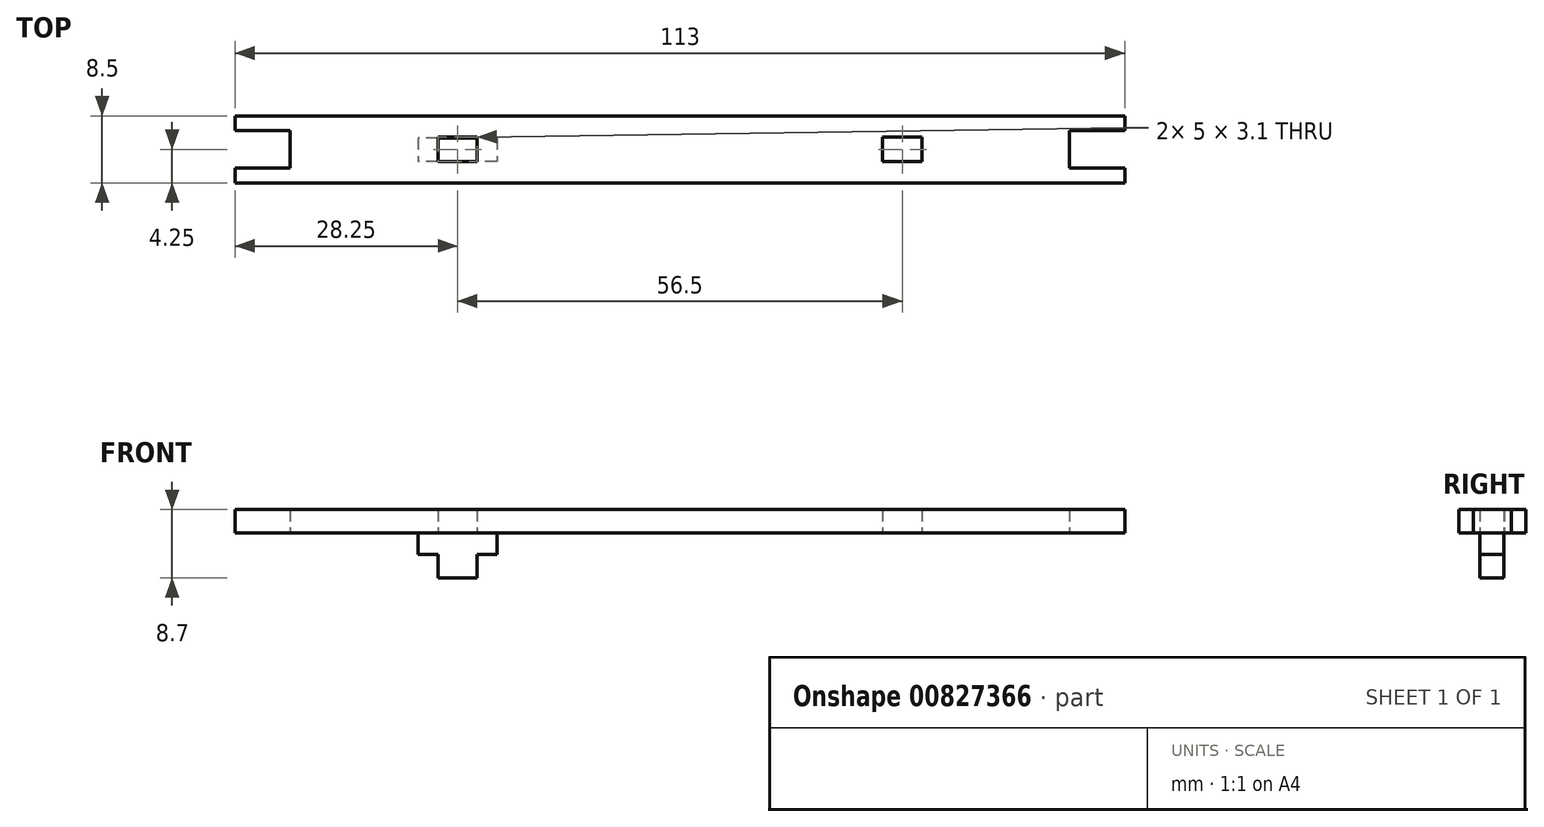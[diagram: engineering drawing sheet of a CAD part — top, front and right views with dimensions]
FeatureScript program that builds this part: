
annotation { "Feature Type Name" : "Feature", "Feature Type Description" : "" }
export const myFeature = defineFeature(function(context is Context, id is Id, definition is map)
    precondition{}
    {
        {
            var Q0;
            Q0=qCreatedBy(makeId("Top.planeOp"),FACE);
            var sketch = newSketch(context, id + "F0", { "sketchPlane" : qUnion([Q0])});
            skLineSegment(sketch, "E0.bottom", {"start": v(0, 4.25) * mm, "end": v(-56.5, 4.25) * mm});
            skLineSegment(sketch, "E0.top", {"start": v(0, -4.25) * mm, "end": v(-56.5, -4.25) * mm});
            skLineSegment(sketch, "E0.left", {"start": v(0, 4.25) * mm, "end": v(0, -4.25) * mm});
            skLineSegment(sketch, "E0.right", {"start": v(-56.5, 4.25) * mm, "end": v(-56.5, -4.25) * mm});
            skPoint(sketch, "E0.middle", {"position": v(-28.25, 0) * mm});
            skCircle(sketch, "E1", {"center": v(-47.98, 8.7) * mm, "radius": 2.6 * mm});
            skCircle(sketch, "E2", {"center": v(-47.98, 8.7) * mm, "radius": 1.35 * mm, "construction": true});
            skLineSegment(sketch, "E3", {"start": v(-50.2, 10.05) * mm, "end": v(-45.76, 10.05) * mm});
            skLineSegment(sketch, "E4.bottom", {"start": v(-25.75, 1.55) * mm, "end": v(-30.75, 1.55) * mm});
            skLineSegment(sketch, "E4.top", {"start": v(-25.75, -1.55) * mm, "end": v(-30.75, -1.55) * mm});
            skLineSegment(sketch, "E4.left", {"start": v(-25.75, 1.55) * mm, "end": v(-25.75, -1.55) * mm});
            skLineSegment(sketch, "E4.right", {"start": v(-30.75, 1.55) * mm, "end": v(-30.75, -1.55) * mm});
            skCircle(sketch, "E5.cCircle", {"center": v(-37.36, 14.34) * mm, "radius": 2.5 * mm, "construction": true});
            skLineSegment(sketch, "E5.0", {"start": v(-35.92, 11.84) * mm, "end": v(-38.8, 11.84) * mm});
            skLineSegment(sketch, "E5.1", {"start": v(-38.8, 11.84) * mm, "end": v(-40.25, 14.34) * mm});
            skLineSegment(sketch, "E5.2", {"start": v(-40.25, 14.34) * mm, "end": v(-38.8, 16.84) * mm});
            skLineSegment(sketch, "E5.3", {"start": v(-38.8, 16.84) * mm, "end": v(-35.92, 16.84) * mm});
            skLineSegment(sketch, "E5.4", {"start": v(-35.92, 16.84) * mm, "end": v(-34.47, 14.34) * mm});
            skLineSegment(sketch, "E5.5", {"start": v(-34.47, 14.34) * mm, "end": v(-35.92, 11.84) * mm});
            skPoint(sketch, "E5.0.midPoint", {"position": v(-37.36, 11.84) * mm});
            skLineSegment(sketch, "E6.bottom", {"start": v(-49.5, 2.4) * mm, "end": v(-63.5, 2.4) * mm});
            skLineSegment(sketch, "E6.top", {"start": v(-49.5, -2.4) * mm, "end": v(-63.5, -2.4) * mm});
            skLineSegment(sketch, "E6.left", {"start": v(-49.5, 2.4) * mm, "end": v(-49.5, -2.4) * mm});
            skLineSegment(sketch, "E6.right", {"start": v(-63.5, 2.4) * mm, "end": v(-63.5, -2.4) * mm});
            skPoint(sketch, "E6.middle", {"position": v(-56.5, 0) * mm});
            skSolve(sketch);
        }
        {
            var Q0;
            {var subQ11=sQuery(id+"F0.wireOp",EDGE,"E0.bottom");Q0=makeQuery(id+"F0.imprint","IMPRINT",FACE,{"disambiguationData":[TD([[makeQuery(id+"F0.imprint","IMPRINT",EDGE,{"derivedFrom":subQ11}),1.0]])]});}
            var Q1;
            {var subQ0=sQuery(id+"F0.wireOp",EDGE,"VcEEM5Fp-5E9m-awkR-xxZw-F9oIajxp1kdQ");Q1=makeQuery(id+"F0.imprint","IMPRINT",FACE,{"disambiguationData":[TD([[makeQuery(id+"F0.imprint","IMPRINT",EDGE,{"derivedFrom":subQ0}),1.0]])]});}
            var Q2;
            {var subQ0=sQuery(id+"F0.wireOp",EDGE,"88a43758-7187-48fa-adfe-aee3dac1ad130.MirrorCS");Q2=makeQuery(id+"F0.imprint","IMPRINT",FACE,{"disambiguationData":[TD([[makeQuery(id+"F0.imprint","IMPRINT",EDGE,{"derivedFrom":subQ0}),-1.0]])]});}
            extrude(context, id + "F1", {"entities" : qUnion([Q0, Q1, Q2]), "depth" : 3 * mm, "offsetDistance" : 25 * mm});
        }
        {
            var Q0;
            Q0=makeQuery(id+"F1.opExtrude","SWEPT_BODY",BODY,{"disambiguationData":[OSD([sQuery(id+"F0.wireOp",EDGE,"E0.bottom"),sQuery(id+"F0.wireOp",EDGE,"E0.top"),sQuery(id+"F0.wireOp",EDGE,"E0.left"),sQuery(id+"F0.wireOp",EDGE,"E0.right"),sQuery(id+"F0.wireOp",EDGE,"XBvBzGPc-q3GS-VzoG-gUGd-wauY02Og8ksk.bottom"),sQuery(id+"F0.wireOp",EDGE,"XBvBzGPc-q3GS-VzoG-gUGd-wauY02Og8ksk.top"),sQuery(id+"F0.wireOp",EDGE,"K85FXUCR-Ngkt-EYOh-FjR8-MBIM410nknZT.bottom"),sQuery(id+"F0.wireOp",EDGE,"K85FXUCR-Ngkt-EYOh-FjR8-MBIM410nknZT.top"),sQuery(id+"F0.wireOp",EDGE,"K85FXUCR-Ngkt-EYOh-FjR8-MBIM410nknZT.right"),sQuery(id+"F0.wireOp",EDGE,"ot6X58GU-7r1Q-ljii-gxMk-kYrKvjyWvYGd"),sQuery(id+"F0.wireOp",EDGE,"E4.bottom"),sQuery(id+"F0.wireOp",EDGE,"E4.top"),sQuery(id+"F0.wireOp",EDGE,"E4.left"),sQuery(id+"F0.wireOp",EDGE,"E4.right")])]});
            var Q1;
            Q1=makeQuery(id+"F1.opExtrude","SWEPT_FACE",FACE,{"disambiguationData":[OSD([sQuery(id+"F0.wireOp",EDGE,"E0.left")])]});
            mirror(context, id + "F2", {"operationType" : NewBodyOperationType.ADD, "entities" : qUnion([Q0]), "mirrorPlane" : qUnion([Q1])});
        }
        {
            var Q0;
            Q0=makeQuery(id+"F1.opExtrude","SWEPT_FACE",FACE,{"disambiguationData":[OSD([sQuery(id+"F0.wireOp",EDGE,"E4.top")])]});
            var sketch = newSketch(context, id + "F3", { "sketchPlane" : qUnion([Q0])});
            skLineSegment(sketch, "E7.0.0", {"start": v(25.75, 0) * mm, "end": v(30.75, 0) * mm});
            skLineSegment(sketch, "E7.0.1", {"start": v(30.75, 0) * mm, "end": v(30.75, 3) * mm});
            skLineSegment(sketch, "E7.0.2", {"start": v(30.75, 3) * mm, "end": v(25.75, 3) * mm});
            skLineSegment(sketch, "E7.0.3", {"start": v(25.75, 3) * mm, "end": v(25.75, 0) * mm});
            skLineSegment(sketch, "E8.bottom", {"start": v(23.25, 0) * mm, "end": v(33.25, 0) * mm});
            skLineSegment(sketch, "E8.top", {"start": v(23.25, -2.7) * mm, "end": v(33.25, -2.7) * mm});
            skLineSegment(sketch, "E8.left", {"start": v(23.25, 0) * mm, "end": v(23.25, -2.7) * mm});
            skLineSegment(sketch, "E8.right", {"start": v(33.25, 0) * mm, "end": v(33.25, -2.7) * mm});
            skPoint(sketch, "E8.middle", {"position": v(28.25, -1.35) * mm});
            skPoint(sketch, "E8.middle.positionSnap0", {"position": v(28.25, 0) * mm});
            skPoint(sketch, "E8.centerSnap0", {"position": v(28.25, 0) * mm});
            skLineSegment(sketch, "E9", {"start": v(28.25, -1.35) * mm, "end": v(23.25, -1.35) * mm, "construction": true});
            skLineSegment(sketch, "E10.MirrorCS", {"start": v(30.75, -5.7) * mm, "end": v(25.75, -5.7) * mm});
            skLineSegment(sketch, "E11.MirrorCS", {"start": v(25.75, -5.7) * mm, "end": v(25.75, -2.7) * mm});
            skLineSegment(sketch, "E12.MirrorCS", {"start": v(30.75, -2.7) * mm, "end": v(30.75, -5.7) * mm});
            skSolve(sketch);
        }
        {
            var Q0;
            Q0=makeQuery(id+"F3.imprint","IMPRINT",FACE,{"disambiguationData":[TD([[makeQuery(id+"F3.imprint","IMPRINT",EDGE,{"derivedFrom":sQuery(id+"F3.wireOp",EDGE,"E10.MirrorCS")}),-1.0]])]});
            var Q1;
            {var subQ0=sQuery(id+"F3.wireOp",EDGE,"E8.left");Q1=makeQuery(id+"F3.imprint","IMPRINT",FACE,{"disambiguationData":[TD([[makeQuery(id+"F3.imprint","IMPRINT",EDGE,{"derivedFrom":subQ0}),1.0]])]});}
            var Q2;
            {var subQ0=sQuery(id+"F3.wireOp",EDGE,"E7.0.1");Q2=makeQuery(id+"F3.imprint","IMPRINT",FACE,{"disambiguationData":[TD([[makeQuery(id+"F3.imprint","IMPRINT",EDGE,{"derivedFrom":subQ0}),-1.0]])]});}
            extrude(context, id + "F4", {"entities" : qUnion([Q0, Q1, Q2]), "depth" : 3 * mm, "offsetDistance" : 25 * mm});
        }
    });
